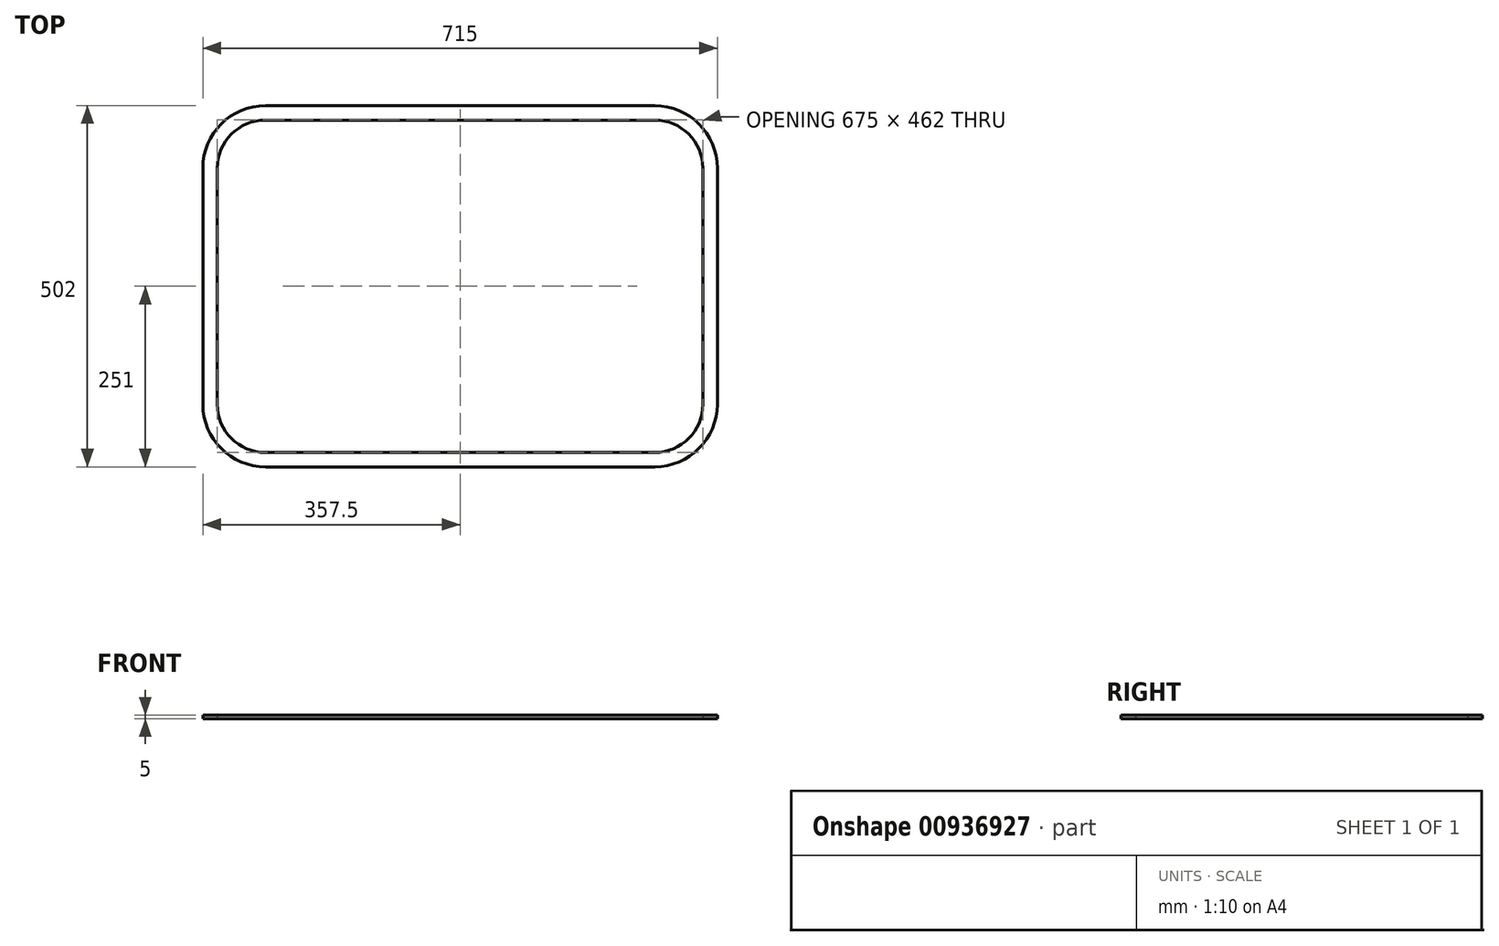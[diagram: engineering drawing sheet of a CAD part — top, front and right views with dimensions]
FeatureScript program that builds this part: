
annotation { "Feature Type Name" : "Feature", "Feature Type Description" : "" }
export const myFeature = defineFeature(function(context is Context, id is Id, definition is map)
    precondition{}
    {
        {
            var Q0;
            Q0=qCreatedBy(makeId("Top.planeOp"),FACE);
            var sketch = newSketch(context, id + "F0", { "sketchPlane" : qUnion([Q0])});
            skLineSegment(sketch, "E0.bottom", {"start": v(270.5, -231) * mm, "end": v(-270.5, -231) * mm});
            skLineSegment(sketch, "E0.top", {"start": v(270.5, 231) * mm, "end": v(-270.5, 231) * mm});
            skLineSegment(sketch, "E0.left", {"start": v(337.5, -164) * mm, "end": v(337.5, 164) * mm});
            skLineSegment(sketch, "E0.right", {"start": v(-337.5, -164) * mm, "end": v(-337.5, 164) * mm});
            skPoint(sketch, "E0.middle", {"position": v(0, 0) * mm});
            skLineSegment(sketch, "E1.bottom", {"start": v(270.5, -251) * mm, "end": v(-270.5, -251) * mm});
            skLineSegment(sketch, "E1.top", {"start": v(270.5, 251) * mm, "end": v(-270.5, 251) * mm});
            skLineSegment(sketch, "E1.left", {"start": v(357.5, -164) * mm, "end": v(357.5, 164) * mm});
            skLineSegment(sketch, "E1.right", {"start": v(-357.5, -164) * mm, "end": v(-357.5, 164) * mm});
            skPoint(sketch, "E2.visualSharp", {"position": v(-337.5, 231) * mm});
            skArc(sketch, "E2.filletArc", {"start": v(-270.5, 231) * mm, "mid": v(-317.88, 211.38) * mm, "end": v(-337.5, 164) * mm});
            skPoint(sketch, "E3.visualSharp", {"position": v(337.5, 231) * mm});
            skArc(sketch, "E3.filletArc", {"start": v(337.5, 164) * mm, "mid": v(317.88, 211.38) * mm, "end": v(270.5, 231) * mm});
            skPoint(sketch, "E4.visualSharp", {"position": v(337.5, -231) * mm});
            skArc(sketch, "E4.filletArc", {"start": v(270.5, -231) * mm, "mid": v(317.88, -211.38) * mm, "end": v(337.5, -164) * mm});
            skPoint(sketch, "E5.visualSharp", {"position": v(-337.5, -231) * mm});
            skArc(sketch, "E5.filletArc", {"start": v(-337.5, -164) * mm, "mid": v(-317.88, -211.38) * mm, "end": v(-270.5, -231) * mm});
            skPoint(sketch, "E6.visualSharp", {"position": v(-357.5, 251) * mm});
            skArc(sketch, "E6.filletArc", {"start": v(-270.5, 251) * mm, "mid": v(-332.02, 225.52) * mm, "end": v(-357.5, 164) * mm});
            skPoint(sketch, "E7.visualSharp", {"position": v(357.5, 251) * mm});
            skArc(sketch, "E7.filletArc", {"start": v(357.5, 164) * mm, "mid": v(332.02, 225.52) * mm, "end": v(270.5, 251) * mm});
            skPoint(sketch, "E8.visualSharp", {"position": v(357.5, -251) * mm});
            skArc(sketch, "E8.filletArc", {"start": v(270.5, -251) * mm, "mid": v(332.02, -225.52) * mm, "end": v(357.5, -164) * mm});
            skPoint(sketch, "E9.visualSharp", {"position": v(-357.5, -251) * mm});
            skArc(sketch, "E9.filletArc", {"start": v(-357.5, -164) * mm, "mid": v(-332.02, -225.52) * mm, "end": v(-270.5, -251) * mm});
            skSolve(sketch);
        }
        {
            var Q0;
            Q0=makeQuery(id+"F0.imprint","IMPRINT",FACE,{"disambiguationData":[TD([[makeQuery(id+"F0.imprint","IMPRINT",EDGE,{"derivedFrom":sQuery(id+"F0.wireOp",EDGE,"E0.bottom")}),1.0]])]});
            extrude(context, id + "F1", {"entities" : qUnion([Q0]), "depth" : 5 * mm, "offsetDistance" : 25 * mm});
        }
    });
